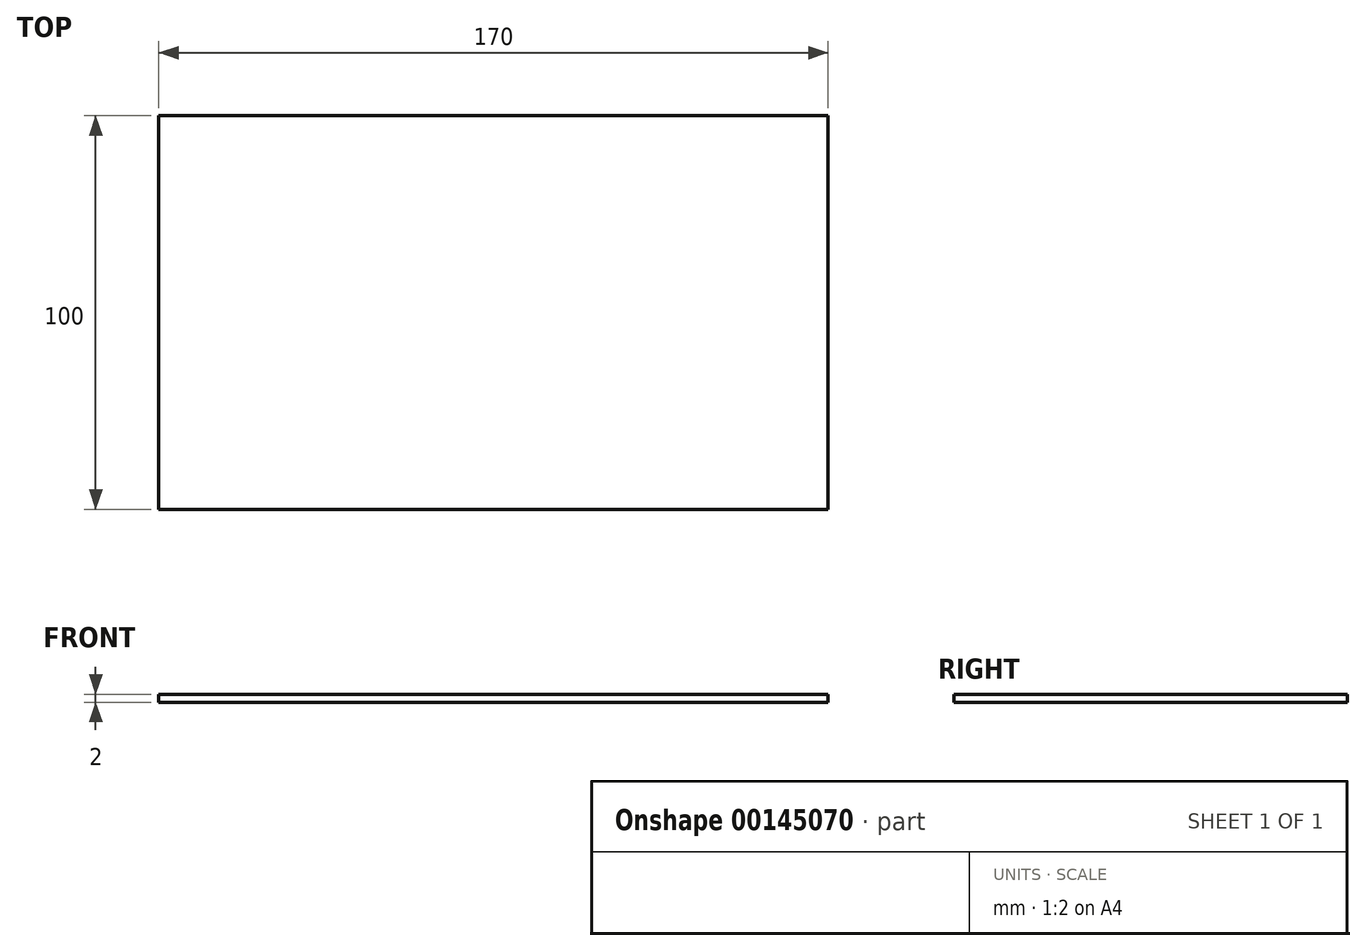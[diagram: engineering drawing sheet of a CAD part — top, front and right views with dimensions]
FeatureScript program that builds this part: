
annotation { "Feature Type Name" : "Feature", "Feature Type Description" : "" }
export const myFeature = defineFeature(function(context is Context, id is Id, definition is map)
    precondition{}
    {
        {
            var Q0;
            Q0=qCreatedBy(makeId("Top.planeOp"),FACE);
            var sketch = newSketch(context, id + "F0", { "sketchPlane" : qUnion([Q0])});
            skLineSegment(sketch, "E0.bottom", {"start": v(0, 0) * mm, "end": v(170, 0) * mm});
            skLineSegment(sketch, "E0.top", {"start": v(0, 100) * mm, "end": v(170, 100) * mm});
            skLineSegment(sketch, "E0.left", {"start": v(0, 0) * mm, "end": v(0, 100) * mm});
            skLineSegment(sketch, "E0.right", {"start": v(170, 0) * mm, "end": v(170, 100) * mm});
            skSolve(sketch);
        }
        {
            var Q0;
            Q0=makeQuery(id+"F0.imprint","IMPRINT",FACE,{"disambiguationData":[TD([[makeQuery(id+"F0.imprint","IMPRINT",EDGE,{"derivedFrom":sQuery(id+"F0.wireOp",EDGE,"E0.bottom")}),1.0]])]});
            extrude(context, id + "F1", {"entities" : qUnion([Q0]), "depth" : 2 * mm});
        }
    });
